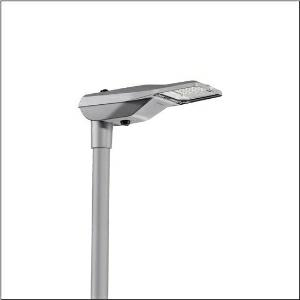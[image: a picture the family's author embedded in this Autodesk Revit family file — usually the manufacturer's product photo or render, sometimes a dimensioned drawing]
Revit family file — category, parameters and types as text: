
# Revit family: streetlight_sl_21_iq_micro___st0_8a_5xe1c31y08cb_ba99
name_source: partatom
category: Lighting Fixtures
units: mm (PartAtom-declared; Revit-internal decimal feet)

## family parameters
Cut with Voids When Loaded = No
Host = Face
Light Source = No
Part Type = Normal
Room Calculation Point = No
Round Connector Dimension = Use Diameter
Shared = No

## types (1)
- --- (1 x LED, 2880 lm, 19.1 W, 3000K)
    Apparent Load = 19 VA
    CIE Flux Codes = 38 75 97 100 100
    Color Rendering = 70
    Color Temperature = 3000K
    Default Elevation = 1800 mm
    Description = Streetlight SL 21 iQ micro, mast luminaire, primary light control with lens, of PMMA, primary optical cover: cover, of toughened safety glass, transparent, light distribution: ST0.8a, light emission: direct distribution, primary light characteristic: asymmetric, installation type: post-top, side-entry, LED, High Power LED, rated luminous flux: 2.880lm, luminous efficacy: 151lm/W, light colour: 730, colour temperature: 3000K, control gear: iQ-Street Remote, D4i with power reduction, control: pre-setting: logarithmic dimming characteristic, Street-Remote, Auto-Match, Temp-Guard, Lumen-Switch, Night-Set, Smart-Wire, Light-Fading, Desk-Remote (wireless, voltage-free reading and setting of iQ features in the workshop via application-optimized NFC function/RFID function), optimised constant luminous flux control (CLO 2.0), mains connection: 220..240V, AC, 50/60Hz, start of lifetime: 19W, end of service life: 20W, reduction: 9W, luminaire housing, of diecast aluminium, powder-coated, Siteco® metallic grey (DB 702S), corrosivity category C5 mid according to DIN EN ISO 12944, please order mast flange separately, inclination adjustable: 0°, 5°, 10°, 15°, sealing non-destructively replaceable, multi-level sealing system, length: 528mm, width: 235mm, height: 110mm, mast flange for spigot size: 42mm (side-entry): 5XC10008XM4, 60/48mm (side-entry/post-top): 5XC10108XM2, 76/60mm (side-entry/post-top): 5XC10108XM1, mounting height: 4..8m, Smart Interface below and above, protection rating (complete): IP66, insulation class (complete): insulation class II (safety insulation), certification: CE, ENEC, ENEC+, VDE, impact resistance: IK10, permissible operating ambient temperature for outdoor applications: -40..+50°C, standard-compliant lighting for roads and squares, packaging unit: 1 piece

Light Distribution: ST0.8a
    Height = 110 mm
    Lamp = 1 x LED
    Lamp Light Flux = 2880 lm
    Lamp Power = 19.1 W
    Lamp count = 1
    Length = 528 mm
    Luminous efficacy = 151 lm/W
    Manufacturer = Siteco
    ModVariant = No
    Model = 5XE1C31Y08CB
    Number of Poles = 1
    OnlyDefault = Yes
    Power Factor = 1
    Product Name = Streetlight SL 21 iQ micro | ST0.8a
    Product group = mast luminaire | pylon top
    ProductGroupID = 6100
    Protection Class = Protection class II
    Protection Degree = IP 66
    RLX_Detail_Level = 1
    RLX_Emergency_Light_Flux = 0 lm
    RLX_Emergency_Type = 0
    RLX_Emergency_Type_DB = No
    RlxData = <blob elided: 99001 chars, md5=0b6c0e70>
    Socket = socket
    Standby Power = 0 W
    System Light Flux = 2880 lm
    System Power = 19 W
    Type Comments = factory setting: luminous flux: 100 % | dim-lin: 254 | 387 mA
    Type Image = l_1007239.jpg
    URL = http://relux.com
    VarID = @adj_113424
    Voltage = 0 V
    Weight = 0.00 kg
    Width = 235 mm

## geometry (parser evidence)
native form markers: Blend x4, Sweep x11
no freeform markers — native parametric forms only
